# Revit family: Plumbing_Drainage_Menzies-Metal_Clamp-Tite_Copper-Drain
name_source: partatom
category: Plumbing Fixtures
revit_build: Autodesk Revit 2015 (Build: 20160512_1515(x64)
units: mm (PartAtom-declared; Revit-internal decimal feet)

## types (3) — shared parameters
Assembly Code = D2040200
Default Elevation = 4' - 0"
Description = Clamp-Tite Spun Copper Drain
Drain Flow = 0 GPM
Edition number = 1
Manufacturer = Menzies Metal Products
Pipe Length = 0' - 11"
Pipe Length Note = Longer pipes available.  Pipes can be field cut to the desired length.
Product Guid = 18a5b31f-90d6-4a0e-9824-848576e72154
Product Material = Metal - Menzies Metal Products - Copper
Product data url = https://bimobject.com
URL = https://www.menzies-metal.com

## per-type parameters (varying)
| type | Model | Weight |
| 2" | 300-3165 | 5.25 lbf |
| 3" | 300-3166 | 5.95 lbf |
| 4" | 300-3167 | 6.50 lbf |

note: column(s) folded — value = type name in every type: Pipe Diameter

## geometry (parser evidence)
native form markers: Sweep x3
no freeform markers — native parametric forms only
